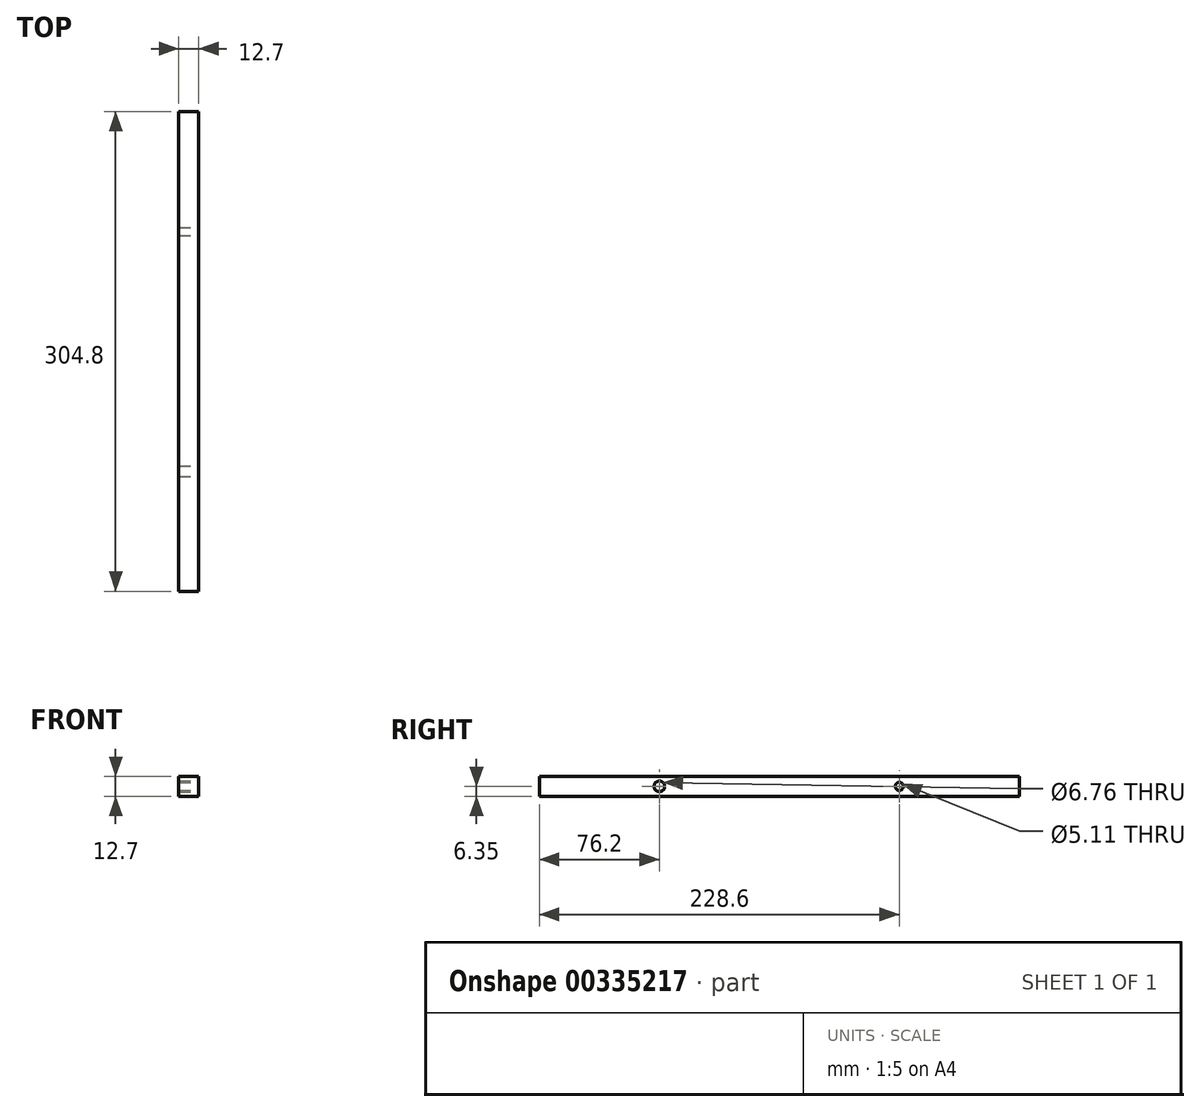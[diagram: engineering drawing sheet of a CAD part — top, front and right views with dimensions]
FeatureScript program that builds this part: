
annotation { "Feature Type Name" : "Feature", "Feature Type Description" : "" }
export const myFeature = defineFeature(function(context is Context, id is Id, definition is map)
    precondition{}
    {
        {
            var Q0;
            Q0=qCreatedBy(makeId("Front.planeOp"),FACE);
            var sketch = newSketch(context, id + "F0", { "sketchPlane" : qUnion([Q0])});
            skLineSegment(sketch, "E0.bottom", {"start": v(0, 0) * mm, "end": v(12.7, 0) * mm});
            skLineSegment(sketch, "E0.top", {"start": v(0, 12.7) * mm, "end": v(12.7, 12.7) * mm});
            skLineSegment(sketch, "E0.left", {"start": v(0, 0) * mm, "end": v(0, 12.7) * mm});
            skLineSegment(sketch, "E0.right", {"start": v(12.7, 0) * mm, "end": v(12.7, 12.7) * mm});
            skSolve(sketch);
        }
        {
            var Q0;
            Q0 = qSketchRegion(id + "F0", true);
            extrude(context, id + "F1", {"entities" : qUnion([Q0]), "depth" : 304.8 * mm});
        }
        {
            var Q0;
            Q0=makeQuery(id+"F1.opExtrude","SWEPT_FACE",FACE,{"disambiguationData":[OSD([sQuery(id+"F0.wireOp",EDGE,"E0.right")])]});
            var sketch = newSketch(context, id + "F2", { "sketchPlane" : qUnion([Q0])});
            skPoint(sketch, "E1", {"position": v(-228.6, 6.35) * mm});
            skPoint(sketch, "E2", {"position": v(-76.2, 6.35) * mm});
            skSolve(sketch);
        }
        {
            var Q0;
            Q0=sQuery(id+"F2.wireOp",VERTEX,"E1");
            var Q1;
            Q1=makeQuery(id+"F1.opExtrude","SWEPT_BODY",BODY,{"disambiguationData":[OSD([sQuery(id+"F0.wireOp",EDGE,"E0.bottom"),sQuery(id+"F0.wireOp",EDGE,"E0.top"),sQuery(id+"F0.wireOp",EDGE,"E0.left"),sQuery(id+"F0.wireOp",EDGE,"E0.right")])]});
            hole(context, id + "F3", {"style" : HoleStyle.SIMPLE, "endStyle" : HoleEndStyle.THROUGH, "standardTappedOrClearance" : lookupTablePath({ "standard" : "ANSI", "fit" : "Normal (ASME)", "size" : "1/4", "type" : "Clearance" }), "standardBlindInLast" : lookupTablePath({ "fit" : "Free", "standard" : "ANSI", "size" : "1/4", "type" : "Clearance" }), "holeDiameter" : 6.76 * mm, "tappedDepth" : 12.7 * mm, "tapClearance" : 3, "locations" : qUnion([Q0]), "scope" : qUnion([Q1])});
        }
        {
            var Q0;
            Q0=sQuery(id+"F2.wireOp",VERTEX,"E2");
            var Q1;
            Q1=makeQuery(id+"F1.opExtrude","SWEPT_BODY",BODY,{"disambiguationData":[OSD([sQuery(id+"F0.wireOp",EDGE,"E0.bottom"),sQuery(id+"F0.wireOp",EDGE,"E0.top"),sQuery(id+"F0.wireOp",EDGE,"E0.left"),sQuery(id+"F0.wireOp",EDGE,"E0.right")])]});
            hole(context, id + "F4", {"style" : HoleStyle.SIMPLE, "endStyle" : HoleEndStyle.THROUGH, "standardTappedOrClearance" : lookupTablePath({ "standard" : "ANSI", "engagement" : "75%", "pitch" : "20 tpi", "size" : "1/4", "type" : "Tapped" }), "standardBlindInLast" : lookupTablePath({ "standard" : "ANSI", "engagement" : "75%", "pitch" : "20 tpi", "size" : "1/4", "type" : "Tapped" }), "holeDiameter" : 5.1 * mm, "showTappedDepth" : true, "tappedDepth" : 12.7 * mm, "tapClearance" : 3, "locations" : qUnion([Q0]), "scope" : qUnion([Q1]), "majorDiameter" : 6.35 * mm});
        }
    });
